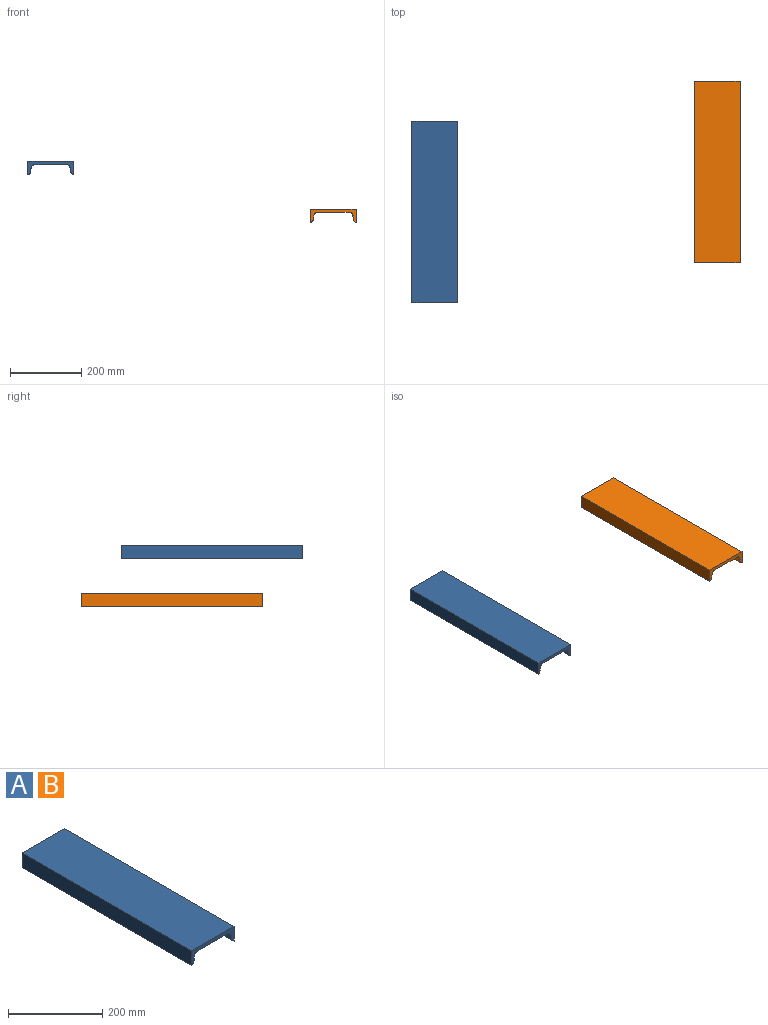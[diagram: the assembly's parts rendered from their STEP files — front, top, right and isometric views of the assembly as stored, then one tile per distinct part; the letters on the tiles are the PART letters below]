
ASSEMBLY  parts=2 mates=2
PART A: 10 faces, bbox 127x508x38 mm
  f0: plane 508x38.05mm, normal (-1,0,0), area 19329mm2, adj f1,f7,f8,f9
  f1: extruded ~508x21.2mm, area 12349.7mm2, adj f0,f2,f8,f9
  f2: cylinder r=11.04mm len=508mm, axis (0,1,0), area 7144.1mm2, adj f1,f3,f8,f9
  f3: plane 508x87.81mm, normal (0,0,-1), area 44609.6mm2, adj f2,f4,f8,f9
  f4: cylinder r=11.04mm len=508mm, axis (0,1,0), area 7144.1mm2, adj f3,f5,f8,f9
  f5: extruded ~508x21.2mm, area 12349.7mm2, adj f4,f6,f8,f9
  f6: plane 508x38.05mm, normal (1,0,0), area 19329mm2, adj f5,f7,f8,f9
  f7: plane 508x127mm, normal (0,0,1), area 64516mm2, adj f0,f6,f8,f9
  f8: plane 127x38.05mm, normal (0,-1,0), area 1611.9mm2, adj f0,f1,f2,f3,f4,f5,f6,f7
  f9: plane 127x38.05mm, normal (0,1,0), area 1611.9mm2, adj f0,f1,f2,f3,f4,f5,f6,f7
PART B: same geometry as A
PLACE A t=(-855.94,96.98,-18.04)mm
PLACE B t=(-63.88,208.74,-151.35)mm
MATE parallel A.f6 <-> B.f0  axis (1,0,0) through (-792.44,-157.02,-18.04)mm
MATE parallel B.f7 <-> A.f7  axis (0,0,1) through (-63.88,208.74,-132.33)mm
